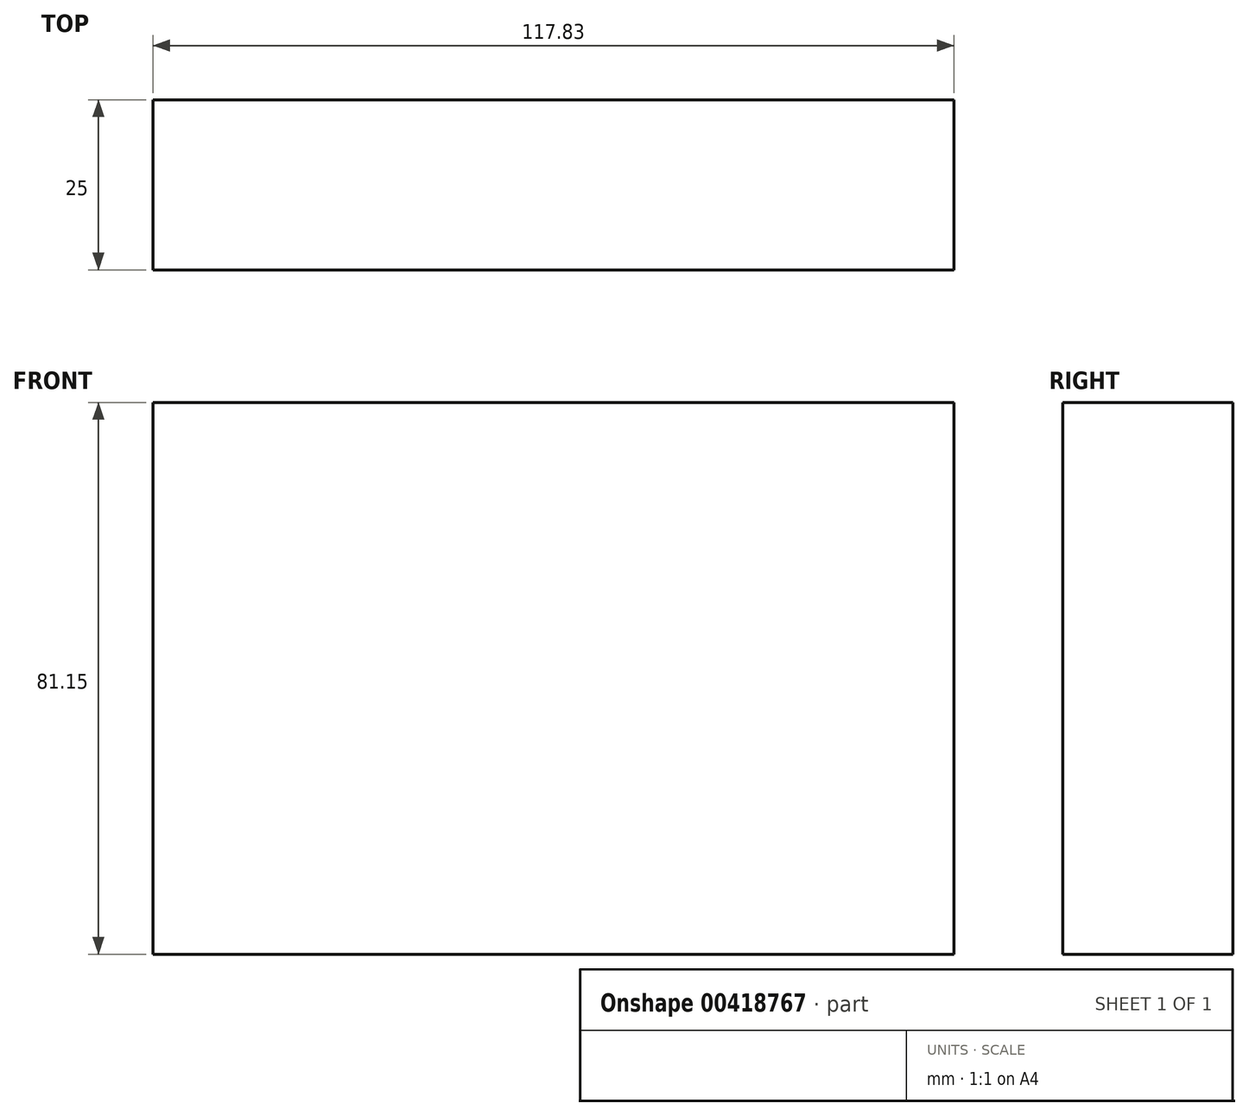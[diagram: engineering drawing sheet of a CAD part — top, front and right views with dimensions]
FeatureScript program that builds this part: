
annotation { "Feature Type Name" : "Feature", "Feature Type Description" : "" }
export const myFeature = defineFeature(function(context is Context, id is Id, definition is map)
    precondition{}
    {
        {
            var Q0;
            Q0=qCreatedBy(makeId("Front.planeOp"),FACE);
            var sketch = newSketch(context, id + "F0", { "sketchPlane" : qUnion([Q0])});
            skLineSegment(sketch, "E0.bottom", {"start": v(-93.13, 48.55) * mm, "end": v(-89.79, 48.55) * mm});
            skLineSegment(sketch, "E0.top", {"start": v(-93.13, 39.84) * mm, "end": v(-89.79, 39.84) * mm});
            skLineSegment(sketch, "E0.left", {"start": v(-93.13, 48.55) * mm, "end": v(-93.13, 39.84) * mm});
            skLineSegment(sketch, "E0.right", {"start": v(-89.79, 48.55) * mm, "end": v(-89.79, 39.84) * mm});
            skLineSegment(sketch, "E1.bottom", {"start": v(-89.79, 39.84) * mm, "end": v(28.04, 39.84) * mm});
            skLineSegment(sketch, "E1.top", {"start": v(-89.79, -41.3) * mm, "end": v(28.04, -41.3) * mm});
            skLineSegment(sketch, "E1.left", {"start": v(-89.79, 39.84) * mm, "end": v(-89.79, -41.3) * mm});
            skLineSegment(sketch, "E1.right", {"start": v(28.04, 39.84) * mm, "end": v(28.04, -41.3) * mm});
            skSolve(sketch);
        }
        {
            var Q0;
            Q0=makeQuery(id+"F0.imprint","IMPRINT",FACE,{"disambiguationData":[TD([[makeQuery(id+"F0.imprint","IMPRINT",EDGE,{"derivedFrom":sQuery(id+"F0.wireOp",EDGE,"E1.bottom")}),-1.0]])]});
            extrude(context, id + "F1", {"entities" : qUnion([Q0]), "depth" : 25 * mm});
        }
    });
